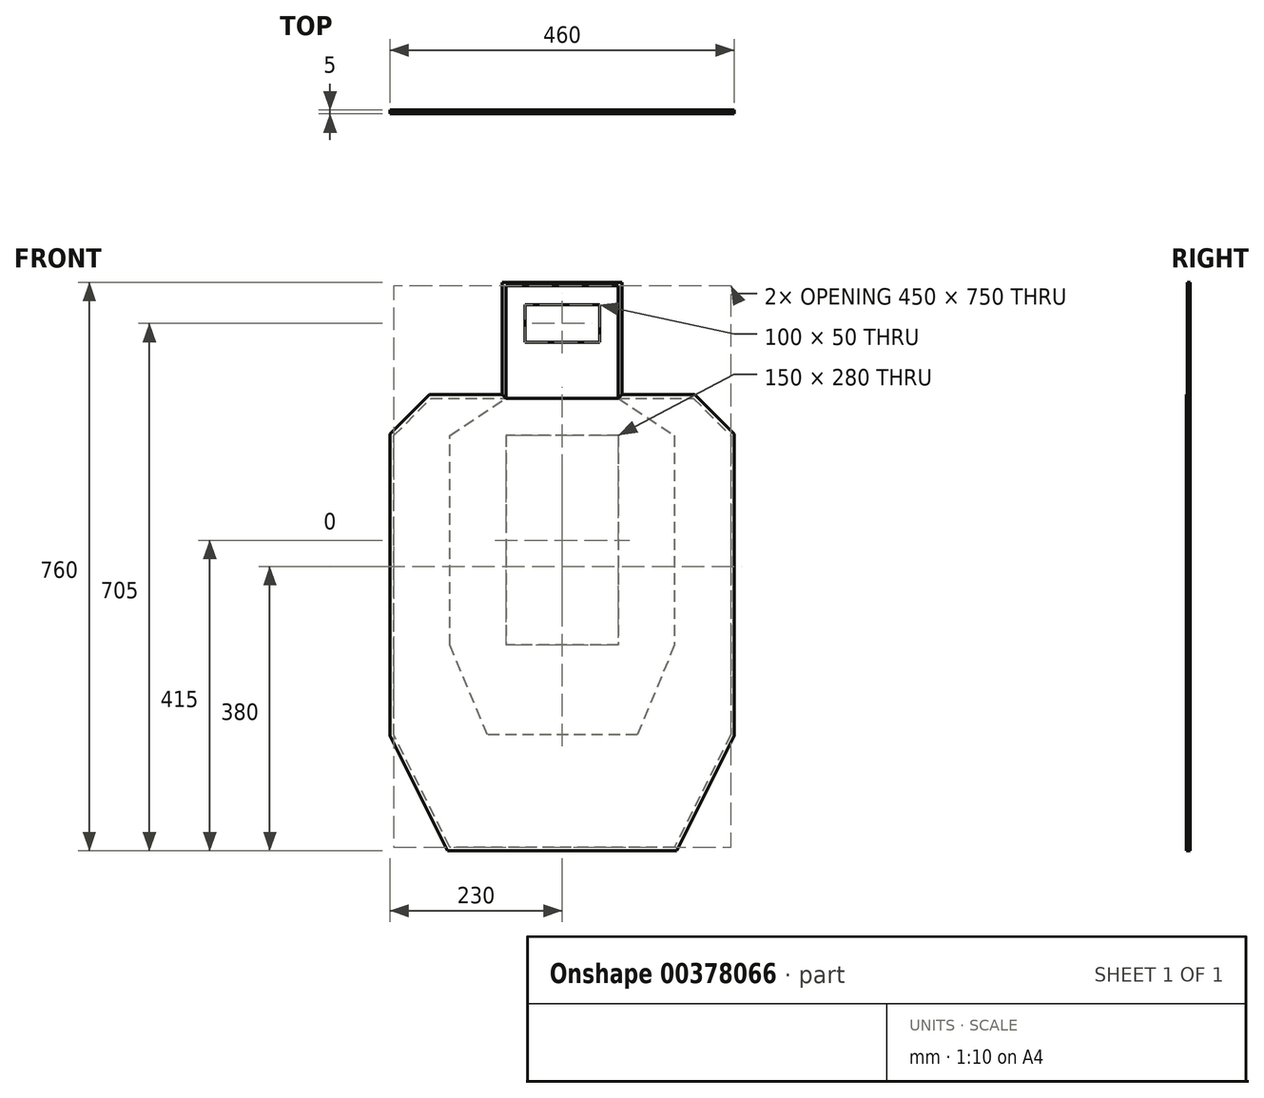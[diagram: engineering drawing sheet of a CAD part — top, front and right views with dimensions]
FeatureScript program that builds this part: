
annotation { "Feature Type Name" : "Feature", "Feature Type Description" : "" }
export const myFeature = defineFeature(function(context is Context, id is Id, definition is map)
    precondition{}
    {
        {
            var Q0;
            Q0=qCreatedBy(makeId("Front.planeOp"),FACE);
            var sketch = newSketch(context, id + "F0", { "sketchPlane" : qUnion([Q0])});
            skLineSegment(sketch, "E0.bottom", {"start": v(0, 100) * mm, "end": v(50, 100) * mm, "construction": true});
            skLineSegment(sketch, "E0.top", {"start": v(0, 125) * mm, "end": v(50, 125) * mm});
            skLineSegment(sketch, "E0.right", {"start": v(50, 100) * mm, "end": v(50, 125) * mm});
            skLineSegment(sketch, "E1.MirrorCS", {"start": v(0, 75) * mm, "end": v(50, 75) * mm});
            skLineSegment(sketch, "E2.MirrorCS", {"start": v(50, 100) * mm, "end": v(50, 75) * mm});
            skLineSegment(sketch, "E3.MirrorCS", {"start": v(0, 0) * mm, "end": v(0, 100) * mm, "construction": true});
            skLineSegment(sketch, "E4.MirrorCS", {"start": v(0, 125) * mm, "end": v(-50, 125) * mm});
            skLineSegment(sketch, "E5.MirrorCS", {"start": v(-50, 100) * mm, "end": v(-50, 125) * mm});
            skLineSegment(sketch, "E6.MirrorCS", {"start": v(-50, 100) * mm, "end": v(-50, 75) * mm});
            skLineSegment(sketch, "E7.MirrorCS", {"start": v(0, 75) * mm, "end": v(-50, 75) * mm});
            skSolve(sketch);
        }
        {
            var Q0;
            Q0=qSketchRegion(id+"F0",true);
            extrude(context, id + "F1", {"entities" : qUnion([Q0]), "oppositeDirection" : true, "depth" : 3 * mm});
        }
        {
            var Q0;
            Q0=qCreatedBy(makeId("Front.planeOp"),FACE);
            var sketch = newSketch(context, id + "F2", { "sketchPlane" : qUnion([Q0])});
            skLineSegment(sketch, "E8", {"start": v(75, 0) * mm, "end": v(75, 150) * mm});
            skLineSegment(sketch, "E9", {"start": v(75, 150) * mm, "end": v(-75, 150) * mm});
            skLineSegment(sketch, "E10", {"start": v(-75, 150) * mm, "end": v(-75, 0) * mm});
            skLineSegment(sketch, "E11", {"start": v(-75, 0) * mm, "end": v(75, 0) * mm});
            skLineSegment(sketch, "E12.0", {"start": v(0, 125) * mm, "end": v(-50, 125) * mm});
            skLineSegment(sketch, "E13.0", {"start": v(0, 125) * mm, "end": v(50, 125) * mm});
            skLineSegment(sketch, "E14.0", {"start": v(50, 100) * mm, "end": v(50, 125) * mm});
            skLineSegment(sketch, "E15.1", {"start": v(50, 100) * mm, "end": v(50, 75) * mm});
            skLineSegment(sketch, "E16.0", {"start": v(0, 75) * mm, "end": v(50, 75) * mm});
            skLineSegment(sketch, "E17.0", {"start": v(0, 75) * mm, "end": v(-50, 75) * mm});
            skLineSegment(sketch, "E18.0", {"start": v(-50, 100) * mm, "end": v(-50, 75) * mm});
            skLineSegment(sketch, "E19.1", {"start": v(-50, 100) * mm, "end": v(-50, 125) * mm});
            skLineSegment(sketch, "E20", {"start": v(0, 125) * mm, "end": v(0, 150) * mm, "construction": true});
            skLineSegment(sketch, "E21", {"start": v(0, 150) * mm, "end": v(0, 137.5) * mm, "construction": true});
            skSolve(sketch);
        }
        {
            var Q0;
            {var subQ0=sQuery(id+"F2.wireOp",EDGE,"E8");Q0=makeQuery(id+"F2.imprint","IMPRINT",FACE,{"disambiguationData":[TD([[makeQuery(id+"F2.imprint","IMPRINT",EDGE,{"derivedFrom":subQ0}),1.0]])]});}
            extrude(context, id + "F3", {"entities" : qUnion([Q0]), "oppositeDirection" : true, "depth" : 3 * mm});
        }
        {
            var Q0;
            Q0=qCreatedBy(makeId("Front.planeOp"),FACE);
            var sketch = newSketch(context, id + "F4", { "sketchPlane" : qUnion([Q0])});
            skLineSegment(sketch, "E22.bottom", {"start": v(75, -50) * mm, "end": v(-75, -50) * mm});
            skLineSegment(sketch, "E22.top", {"start": v(75, -330) * mm, "end": v(-75, -330) * mm});
            skLineSegment(sketch, "E22.left", {"start": v(75, -50) * mm, "end": v(75, -330) * mm});
            skLineSegment(sketch, "E22.right", {"start": v(-75, -50) * mm, "end": v(-75, -330) * mm});
            skLineSegment(sketch, "E23", {"start": v(0, 0) * mm, "end": v(0, -50) * mm, "construction": true});
            skLineSegment(sketch, "E24.0", {"start": v(-75, 0) * mm, "end": v(75, 0) * mm, "construction": true});
            skLineSegment(sketch, "E25", {"start": v(75, 0) * mm, "end": v(75, -50) * mm, "construction": true});
            skSolve(sketch);
        }
        {
            var Q0;
            Q0=makeQuery(id+"F4.imprint","IMPRINT",FACE,{"disambiguationData":[TD([[makeQuery(id+"F4.imprint","IMPRINT",EDGE,{"derivedFrom":sQuery(id+"F4.wireOp",EDGE,"E22.bottom")}),1.0]])]});
            extrude(context, id + "F5", {"entities" : qUnion([Q0]), "oppositeDirection" : true, "depth" : 3 * mm});
        }
        {
            var Q0;
            Q0=qCreatedBy(makeId("Front.planeOp"),FACE);
            var sketch = newSketch(context, id + "F6", { "sketchPlane" : qUnion([Q0])});
            skLineSegment(sketch, "E26.0", {"start": v(-75, 0) * mm, "end": v(75, 0) * mm});
            skLineSegment(sketch, "E27.1", {"start": v(75, -50) * mm, "end": v(75, -330) * mm});
            skLineSegment(sketch, "E28.2", {"start": v(75, -50) * mm, "end": v(-75, -50) * mm});
            skLineSegment(sketch, "E29.3", {"start": v(-75, -50) * mm, "end": v(-75, -330) * mm});
            skLineSegment(sketch, "E30.0", {"start": v(75, -330) * mm, "end": v(-75, -330) * mm});
            skLineSegment(sketch, "E31", {"start": v(75, 0) * mm, "end": v(150, -50) * mm});
            skLineSegment(sketch, "E32", {"start": v(150, -50) * mm, "end": v(150, -330) * mm});
            skLineSegment(sketch, "E33", {"start": v(150, -330) * mm, "end": v(100, -450) * mm});
            skLineSegment(sketch, "E34", {"start": v(100, -450) * mm, "end": v(-100, -450) * mm});
            skLineSegment(sketch, "E35", {"start": v(-100, -450) * mm, "end": v(-150, -330) * mm});
            skLineSegment(sketch, "E36", {"start": v(-150, -330) * mm, "end": v(-150, -50) * mm});
            skLineSegment(sketch, "E37", {"start": v(-150, -50) * mm, "end": v(-75, 0) * mm});
            skLineSegment(sketch, "E38", {"start": v(0, -450) * mm, "end": v(0, -50) * mm, "construction": true});
            skLineSegment(sketch, "E39", {"start": v(150, -50) * mm, "end": v(75, -50) * mm, "construction": true});
            skLineSegment(sketch, "E40", {"start": v(-55.04, -50) * mm, "end": v(-150, -50) * mm, "construction": true});
            skLineSegment(sketch, "E41", {"start": v(150, -330) * mm, "end": v(150, -450) * mm, "construction": true});
            skLineSegment(sketch, "E42", {"start": v(100, -450) * mm, "end": v(150, -450) * mm, "construction": true});
            skLineSegment(sketch, "E43", {"start": v(150, -330) * mm, "end": v(-150, -330) * mm, "construction": true});
            skLineSegment(sketch, "E44", {"start": v(-150, -330) * mm, "end": v(-150, -450) * mm, "construction": true});
            skLineSegment(sketch, "E45", {"start": v(-150, -450) * mm, "end": v(-100, -450) * mm, "construction": true});
            skSolve(sketch);
        }
        {
            var Q0;
            Q0=makeQuery(id+"F6.imprint","IMPRINT",FACE,{"disambiguationData":[TD([[makeQuery(id+"F6.imprint","IMPRINT",EDGE,{"derivedFrom":sQuery(id+"F6.wireOp",EDGE,"E26.0")}),-1.0]])]});
            extrude(context, id + "F7", {"entities" : qUnion([Q0]), "oppositeDirection" : true, "depth" : 3 * mm});
        }
        {
            var Q0;
            Q0=makeQuery(id+"F7.opExtrude","CAP_FACE",FACE,{"disambiguationData":[OSD([sQuery(id+"F6.wireOp",EDGE,"E26.0"),sQuery(id+"F6.wireOp",EDGE,"E27.1"),sQuery(id+"F6.wireOp",EDGE,"E28.2"),sQuery(id+"F6.wireOp",EDGE,"E29.3"),sQuery(id+"F6.wireOp",EDGE,"E30.0"),sQuery(id+"F6.wireOp",EDGE,"E31"),sQuery(id+"F6.wireOp",EDGE,"E32"),sQuery(id+"F6.wireOp",EDGE,"E33"),sQuery(id+"F6.wireOp",EDGE,"E34"),sQuery(id+"F6.wireOp",EDGE,"E35"),sQuery(id+"F6.wireOp",EDGE,"E36"),sQuery(id+"F6.wireOp",EDGE,"E37")])],"isStart":true});
            var sketch = newSketch(context, id + "F8", { "sketchPlane" : qUnion([Q0])});
            skLineSegment(sketch, "E46.0", {"start": v(75, 0) * mm, "end": v(150, -50) * mm});
            skLineSegment(sketch, "E47.0", {"start": v(150, -50) * mm, "end": v(150, -330) * mm});
            skLineSegment(sketch, "E48.0", {"start": v(150, -330) * mm, "end": v(100, -450) * mm});
            skLineSegment(sketch, "E49.1", {"start": v(100, -450) * mm, "end": v(-100, -450) * mm});
            skLineSegment(sketch, "E50.0", {"start": v(-150, -330) * mm, "end": v(-150, -50) * mm});
            skLineSegment(sketch, "E51.0", {"start": v(-100, -450) * mm, "end": v(-150, -330) * mm});
            skLineSegment(sketch, "E52.0", {"start": v(-150, -50) * mm, "end": v(-75, 0) * mm});
            skLineSegment(sketch, "E53", {"start": v(75, 0) * mm, "end": v(175, 0) * mm});
            skLineSegment(sketch, "E54", {"start": v(175, 0) * mm, "end": v(225, -50) * mm});
            skLineSegment(sketch, "E55", {"start": v(225, -50) * mm, "end": v(225, -450) * mm});
            skLineSegment(sketch, "E56", {"start": v(225, -450) * mm, "end": v(150, -600) * mm});
            skLineSegment(sketch, "E57", {"start": v(150, -600) * mm, "end": v(-150, -600) * mm});
            skLineSegment(sketch, "E58", {"start": v(-150, -600) * mm, "end": v(-225, -450) * mm});
            skLineSegment(sketch, "E59", {"start": v(-225, -450) * mm, "end": v(-225, -50) * mm});
            skLineSegment(sketch, "E60", {"start": v(-225, -50) * mm, "end": v(-175, 0) * mm});
            skLineSegment(sketch, "E61", {"start": v(-175, 0) * mm, "end": v(-75, 0) * mm});
            skLineSegment(sketch, "E62", {"start": v(225, -50) * mm, "end": v(225, 0) * mm, "construction": true});
            skLineSegment(sketch, "E63", {"start": v(225, 0) * mm, "end": v(175, 0) * mm, "construction": true});
            skLineSegment(sketch, "E64", {"start": v(225, -450) * mm, "end": v(225, -600) * mm, "construction": true});
            skLineSegment(sketch, "E65", {"start": v(225, -600) * mm, "end": v(150, -600) * mm, "construction": true});
            skLineSegment(sketch, "E66", {"start": v(-225, -450) * mm, "end": v(-225, -600) * mm, "construction": true});
            skLineSegment(sketch, "E67", {"start": v(-225, -600) * mm, "end": v(-150, -600) * mm, "construction": true});
            skLineSegment(sketch, "E68", {"start": v(-175, 0) * mm, "end": v(-225, 0) * mm, "construction": true});
            skLineSegment(sketch, "E69", {"start": v(-225, 0) * mm, "end": v(-225, -50) * mm, "construction": true});
            skSolve(sketch);
        }
        {
            var Q0;
            Q0=qSketchRegion(id+"F8",true);
            extrude(context, id + "F9", {"entities" : qUnion([Q0]), "oppositeDirection" : true, "depth" : 3 * mm});
        }
        {
            var Q0;
            Q0=makeQuery(id+"F9.opExtrude","CAP_FACE",FACE,{"disambiguationData":[OSD([sQuery(id+"F8.wireOp",EDGE,"E46.0"),sQuery(id+"F8.wireOp",EDGE,"E47.0"),sQuery(id+"F8.wireOp",EDGE,"E48.0"),sQuery(id+"F8.wireOp",EDGE,"E49.1"),sQuery(id+"F8.wireOp",EDGE,"E50.0"),sQuery(id+"F8.wireOp",EDGE,"E51.0"),sQuery(id+"F8.wireOp",EDGE,"E52.0"),sQuery(id+"F8.wireOp",EDGE,"E53"),sQuery(id+"F8.wireOp",EDGE,"E54"),sQuery(id+"F8.wireOp",EDGE,"E55"),sQuery(id+"F8.wireOp",EDGE,"E56"),sQuery(id+"F8.wireOp",EDGE,"E57"),sQuery(id+"F8.wireOp",EDGE,"E58"),sQuery(id+"F8.wireOp",EDGE,"E59"),sQuery(id+"F8.wireOp",EDGE,"E60"),sQuery(id+"F8.wireOp",EDGE,"E61")])],"isStart":true});
            var sketch = newSketch(context, id + "F10", { "sketchPlane" : qUnion([Q0])});
            skLineSegment(sketch, "E70.0", {"start": v(75, 150) * mm, "end": v(-75, 150) * mm});
            skLineSegment(sketch, "E71.0", {"start": v(75, 0) * mm, "end": v(75, 150) * mm});
            skLineSegment(sketch, "E72.1", {"start": v(75, 0) * mm, "end": v(175, 0) * mm});
            skLineSegment(sketch, "E73.0", {"start": v(175, 0) * mm, "end": v(225, -50) * mm});
            skLineSegment(sketch, "E74.1", {"start": v(225, -50) * mm, "end": v(225, -450) * mm});
            skLineSegment(sketch, "E75.0", {"start": v(225, -450) * mm, "end": v(150, -600) * mm});
            skLineSegment(sketch, "E76.1", {"start": v(150, -600) * mm, "end": v(-150, -600) * mm});
            skLineSegment(sketch, "E77.2", {"start": v(-150, -600) * mm, "end": v(-225, -450) * mm});
            skLineSegment(sketch, "E78.3", {"start": v(-225, -450) * mm, "end": v(-225, -50) * mm});
            skLineSegment(sketch, "E79.4", {"start": v(-225, -50) * mm, "end": v(-175, 0) * mm});
            skLineSegment(sketch, "E80.5", {"start": v(-175, 0) * mm, "end": v(-75, 0) * mm});
            skLineSegment(sketch, "E81.0", {"start": v(-75, 150) * mm, "end": v(-75, 0) * mm});
            skLineSegment(sketch, "E82.0", {"start": v(177.07, 5) * mm, "end": v(230, -47.93) * mm});
            skLineSegment(sketch, "E82.1", {"start": v(-230, -451.18) * mm, "end": v(-230, -47.93) * mm});
            skLineSegment(sketch, "E82.2", {"start": v(-153.1, -605) * mm, "end": v(-230, -451.18) * mm});
            skLineSegment(sketch, "E82.3", {"start": v(153.1, -605) * mm, "end": v(-153.1, -605) * mm});
            skLineSegment(sketch, "E82.4", {"start": v(230, -451.18) * mm, "end": v(153.1, -605) * mm});
            skLineSegment(sketch, "E82.5", {"start": v(-230, -47.93) * mm, "end": v(-177.07, 5) * mm});
            skLineSegment(sketch, "E82.6", {"start": v(230, -47.93) * mm, "end": v(230, -451.18) * mm});
            skLineSegment(sketch, "E82.7", {"start": v(-177.07, 5) * mm, "end": v(-80, 5) * mm});
            skLineSegment(sketch, "E82.8", {"start": v(-80, 155) * mm, "end": v(-80, 5) * mm});
            skLineSegment(sketch, "E82.9", {"start": v(80, 155) * mm, "end": v(-80, 155) * mm});
            skLineSegment(sketch, "E82.10", {"start": v(80, 5) * mm, "end": v(80, 155) * mm});
            skLineSegment(sketch, "E82.11", {"start": v(80, 5) * mm, "end": v(177.07, 5) * mm});
            skSolve(sketch);
        }
        {
            var Q0;
            Q0=makeQuery(id+"F10.imprint","IMPRINT",FACE,{"disambiguationData":[TD([[makeQuery(id+"F10.imprint","IMPRINT",EDGE,{"derivedFrom":sQuery(id+"F10.wireOp",EDGE,"E70.0")}),-1.0]])]});
            extrude(context, id + "F11", {"entities" : qUnion([Q0]), "oppositeDirection" : true, "depth" : 3 * mm});
        }
        {
            var Q0;
            Q0=makeQuery(id+"F9.opExtrude","CAP_FACE",FACE,{"disambiguationData":[OSD([sQuery(id+"F8.wireOp",EDGE,"E46.0"),sQuery(id+"F8.wireOp",EDGE,"E47.0"),sQuery(id+"F8.wireOp",EDGE,"E48.0"),sQuery(id+"F8.wireOp",EDGE,"E49.1"),sQuery(id+"F8.wireOp",EDGE,"E50.0"),sQuery(id+"F8.wireOp",EDGE,"E51.0"),sQuery(id+"F8.wireOp",EDGE,"E52.0"),sQuery(id+"F8.wireOp",EDGE,"E53"),sQuery(id+"F8.wireOp",EDGE,"E54"),sQuery(id+"F8.wireOp",EDGE,"E55"),sQuery(id+"F8.wireOp",EDGE,"E56"),sQuery(id+"F8.wireOp",EDGE,"E57"),sQuery(id+"F8.wireOp",EDGE,"E58"),sQuery(id+"F8.wireOp",EDGE,"E59"),sQuery(id+"F8.wireOp",EDGE,"E60"),sQuery(id+"F8.wireOp",EDGE,"E61")])],"isStart":false});
            var sketch = newSketch(context, id + "F12", { "sketchPlane" : qUnion([Q0])});
            skLineSegment(sketch, "E83.0", {"start": v(75, 150) * mm, "end": v(75, 0) * mm});
            skLineSegment(sketch, "E84.0", {"start": v(175, 0) * mm, "end": v(75, 0) * mm});
            skLineSegment(sketch, "E85.0", {"start": v(-75, 150) * mm, "end": v(75, 150) * mm});
            skLineSegment(sketch, "E86.0", {"start": v(225, -50) * mm, "end": v(175, 0) * mm});
            skLineSegment(sketch, "E87.0", {"start": v(-225, -50) * mm, "end": v(-225, -450) * mm});
            skLineSegment(sketch, "E87.1", {"start": v(225, -450) * mm, "end": v(225, -50) * mm});
            skLineSegment(sketch, "E87.2", {"start": v(150, -600) * mm, "end": v(225, -450) * mm});
            skLineSegment(sketch, "E87.3", {"start": v(-225, -450) * mm, "end": v(-150, -600) * mm});
            skLineSegment(sketch, "E87.4", {"start": v(-150, -600) * mm, "end": v(150, -600) * mm});
            skLineSegment(sketch, "E88.0", {"start": v(-175, 0) * mm, "end": v(-225, -50) * mm});
            skLineSegment(sketch, "E89.0", {"start": v(-75, 0) * mm, "end": v(-175, 0) * mm});
            skLineSegment(sketch, "E90.0", {"start": v(-75, 0) * mm, "end": v(-75, 150) * mm});
            skSolve(sketch);
        }
        {
            var Q0;
            Q0=qSketchRegion(id+"F12",true);
            extrude(context, id + "F13", {"entities" : qUnion([Q0]), "depth" : 1 * mm});
        }
        {
            var Q0;
            Q0=makeQuery(id+"F13.opExtrude","CAP_FACE",FACE,{"disambiguationData":[OSD([sQuery(id+"F12.wireOp",EDGE,"E83.0"),sQuery(id+"F12.wireOp",EDGE,"E84.0"),sQuery(id+"F12.wireOp",EDGE,"E85.0"),sQuery(id+"F12.wireOp",EDGE,"E86.0"),sQuery(id+"F12.wireOp",EDGE,"E87.0"),sQuery(id+"F12.wireOp",EDGE,"E87.1"),sQuery(id+"F12.wireOp",EDGE,"E87.2"),sQuery(id+"F12.wireOp",EDGE,"E87.3"),sQuery(id+"F12.wireOp",EDGE,"E87.4"),sQuery(id+"F12.wireOp",EDGE,"E88.0"),sQuery(id+"F12.wireOp",EDGE,"E89.0"),sQuery(id+"F12.wireOp",EDGE,"E90.0")])],"isStart":false});
            var sketch = newSketch(context, id + "F14", { "sketchPlane" : qUnion([Q0])});
            skLineSegment(sketch, "E91.0", {"start": v(-80, 155) * mm, "end": v(80, 155) * mm});
            skLineSegment(sketch, "E92.0", {"start": v(80, 155) * mm, "end": v(80, 5) * mm});
            skLineSegment(sketch, "E93.0", {"start": v(-80, 5) * mm, "end": v(-80, 155) * mm});
            skLineSegment(sketch, "E94.0", {"start": v(177.07, 5) * mm, "end": v(80, 5) * mm});
            skLineSegment(sketch, "E95.0", {"start": v(-80, 5) * mm, "end": v(-177.07, 5) * mm});
            skLineSegment(sketch, "E96.0", {"start": v(230, -47.93) * mm, "end": v(177.07, 5) * mm});
            skLineSegment(sketch, "E97.0", {"start": v(-177.07, 5) * mm, "end": v(-230, -47.93) * mm});
            skLineSegment(sketch, "E98.1", {"start": v(-230, -47.93) * mm, "end": v(-230, -451.18) * mm});
            skLineSegment(sketch, "E99.0", {"start": v(-230, -451.18) * mm, "end": v(-153.1, -605) * mm});
            skLineSegment(sketch, "E100.0", {"start": v(-153.1, -605) * mm, "end": v(153.1, -605) * mm});
            skLineSegment(sketch, "E101.0", {"start": v(153.1, -605) * mm, "end": v(230, -451.18) * mm});
            skLineSegment(sketch, "E102.0", {"start": v(230, -451.18) * mm, "end": v(230, -47.93) * mm});
            skLineSegment(sketch, "E103.0", {"start": v(-75, 150) * mm, "end": v(75, 150) * mm});
            skLineSegment(sketch, "E104.0", {"start": v(-75, 0) * mm, "end": v(-75, 150) * mm});
            skLineSegment(sketch, "E105.0", {"start": v(75, 150) * mm, "end": v(75, 0) * mm});
            skLineSegment(sketch, "E106.0", {"start": v(175, 0) * mm, "end": v(75, 0) * mm});
            skLineSegment(sketch, "E107.0", {"start": v(225, -50) * mm, "end": v(175, 0) * mm});
            skLineSegment(sketch, "E108.0", {"start": v(150, -600) * mm, "end": v(225, -450) * mm});
            skLineSegment(sketch, "E109.0", {"start": v(225, -450) * mm, "end": v(225, -50) * mm});
            skLineSegment(sketch, "E110.0", {"start": v(-150, -600) * mm, "end": v(150, -600) * mm});
            skLineSegment(sketch, "E111.0", {"start": v(-225, -450) * mm, "end": v(-150, -600) * mm});
            skLineSegment(sketch, "E112.0", {"start": v(-225, -50) * mm, "end": v(-225, -450) * mm});
            skLineSegment(sketch, "E113.0", {"start": v(-175, 0) * mm, "end": v(-225, -50) * mm});
            skLineSegment(sketch, "E114.0", {"start": v(-75, 0) * mm, "end": v(-175, 0) * mm});
            skSolve(sketch);
        }
        {
            var Q0;
            Q0=makeQuery(id+"F14.imprint","IMPRINT",FACE,{"disambiguationData":[TD([[makeQuery(id+"F14.imprint","IMPRINT",EDGE,{"derivedFrom":sQuery(id+"F14.wireOp",EDGE,"E91.0")}),-1.0]])]});
            extrude(context, id + "F15", {"entities" : qUnion([Q0]), "oppositeDirection" : true, "depth" : 1 * mm});
        }
        {
            var Q0;
            Q0=makeQuery(id+"F9.opExtrude","CAP_FACE",FACE,{"disambiguationData":[OSD([sQuery(id+"F8.wireOp",EDGE,"E46.0"),sQuery(id+"F8.wireOp",EDGE,"E47.0"),sQuery(id+"F8.wireOp",EDGE,"E48.0"),sQuery(id+"F8.wireOp",EDGE,"E49.1"),sQuery(id+"F8.wireOp",EDGE,"E50.0"),sQuery(id+"F8.wireOp",EDGE,"E51.0"),sQuery(id+"F8.wireOp",EDGE,"E52.0"),sQuery(id+"F8.wireOp",EDGE,"E53"),sQuery(id+"F8.wireOp",EDGE,"E54"),sQuery(id+"F8.wireOp",EDGE,"E55"),sQuery(id+"F8.wireOp",EDGE,"E56"),sQuery(id+"F8.wireOp",EDGE,"E57"),sQuery(id+"F8.wireOp",EDGE,"E58"),sQuery(id+"F8.wireOp",EDGE,"E59"),sQuery(id+"F8.wireOp",EDGE,"E60"),sQuery(id+"F8.wireOp",EDGE,"E61")])],"isStart":true});
            var sketch = newSketch(context, id + "F16", { "sketchPlane" : qUnion([Q0])});
            skLineSegment(sketch, "E115.0", {"start": v(-153.1, -605) * mm, "end": v(-230, -451.18) * mm});
            skLineSegment(sketch, "E116.0", {"start": v(153.1, -605) * mm, "end": v(-153.1, -605) * mm});
            skLineSegment(sketch, "E117.0", {"start": v(230, -451.18) * mm, "end": v(153.1, -605) * mm});
            skLineSegment(sketch, "E118.0", {"start": v(230, -47.93) * mm, "end": v(230, -451.18) * mm});
            skLineSegment(sketch, "E119.0", {"start": v(80, 5) * mm, "end": v(177.07, 5) * mm});
            skLineSegment(sketch, "E119.1", {"start": v(177.07, 5) * mm, "end": v(230, -47.93) * mm});
            skLineSegment(sketch, "E120.0", {"start": v(-75, 0) * mm, "end": v(75, 0) * mm});
            skLineSegment(sketch, "E121.0", {"start": v(-177.07, 5) * mm, "end": v(-80, 5) * mm});
            skLineSegment(sketch, "E122.0", {"start": v(-230, -47.93) * mm, "end": v(-177.07, 5) * mm});
            skLineSegment(sketch, "E123.0", {"start": v(-230, -451.18) * mm, "end": v(-230, -47.93) * mm});
            skLineSegment(sketch, "E124", {"start": v(-80, 5) * mm, "end": v(-75, 0) * mm});
            skLineSegment(sketch, "E125", {"start": v(75, 0) * mm, "end": v(80, 5) * mm});
            skSolve(sketch);
        }
        {
            var Q0;
            Q0=qSketchRegion(id+"F16",true);
            extrude(context, id + "F17", {"entities" : qUnion([Q0]), "depth" : 1 * mm});
        }
    });
